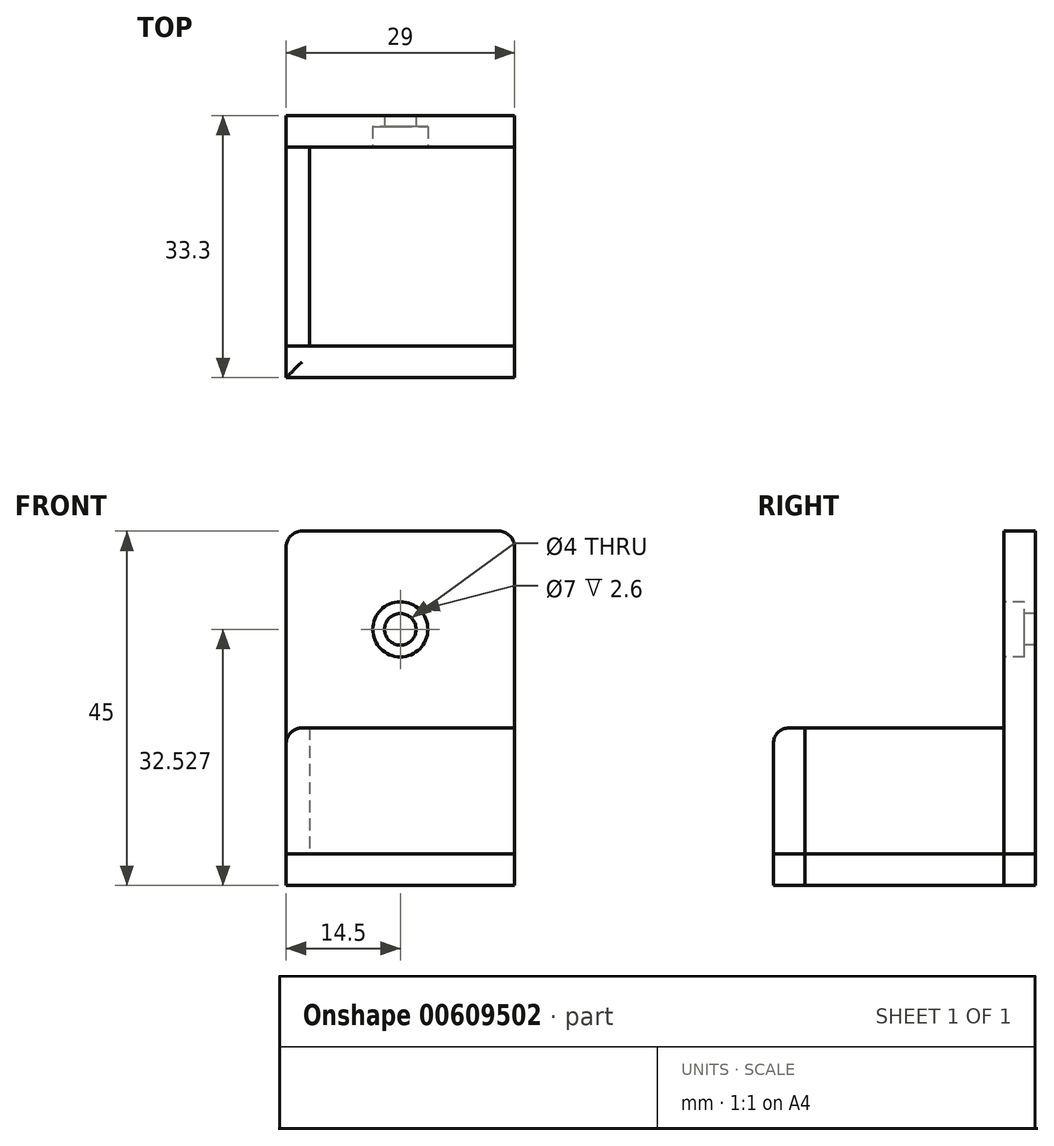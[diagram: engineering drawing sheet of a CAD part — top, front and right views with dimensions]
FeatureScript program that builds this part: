
annotation { "Feature Type Name" : "Feature", "Feature Type Description" : "" }
export const myFeature = defineFeature(function(context is Context, id is Id, definition is map)
    precondition{}
    {
        {
            var Q0;
            Q0=qCreatedBy(makeId("Top.planeOp"),FACE);
            var sketch = newSketch(context, id + "F0", { "sketchPlane" : qUnion([Q0])});
            skLineSegment(sketch, "E0.bottom", {"start": v(14.5, -16.65) * mm, "end": v(-14.5, -16.65) * mm});
            skLineSegment(sketch, "E0.top", {"start": v(14.5, 16.65) * mm, "end": v(-14.5, 16.65) * mm});
            skLineSegment(sketch, "E0.left", {"start": v(14.5, -16.65) * mm, "end": v(14.5, 16.65) * mm});
            skLineSegment(sketch, "E0.right", {"start": v(-14.5, -16.65) * mm, "end": v(-14.5, 16.65) * mm});
            skPoint(sketch, "E0.middle", {"position": v(0, 0) * mm});
            skSolve(sketch);
        }
        {
            var Q0;
            Q0 = qSketchRegion(id + "F0", true);
            extrude(context, id + "F1", {"entities" : qUnion([Q0]), "depth" : 4 * mm, "offsetDistance" : 25 * mm});
        }
        {
            var Q0;
            Q0=makeQuery(id+"F0.imprint","IMPRINT",FACE,{"disambiguationData":[TD([[makeQuery(id+"F0.imprint","IMPRINT",EDGE,{"derivedFrom":sQuery(id+"F0.wireOp",EDGE,"E0.bottom")}),-1.0]])]});
            var sketch = newSketch(context, id + "F2", { "sketchPlane" : qUnion([Q0])});
            skLineSegment(sketch, "E1.bottom", {"start": v(-14.5, 16.65) * mm, "end": v(14.5, 16.65) * mm});
            skLineSegment(sketch, "E1.top", {"start": v(-14.5, 12.65) * mm, "end": v(14.5, 12.65) * mm});
            skLineSegment(sketch, "E1.left", {"start": v(-14.5, 16.65) * mm, "end": v(-14.5, 12.65) * mm});
            skLineSegment(sketch, "E1.right", {"start": v(14.5, 16.65) * mm, "end": v(14.5, 12.65) * mm});
            skSolve(sketch);
        }
        {
            var Q0;
            Q0 = qSketchRegion(id + "F2", true);
            extrude(context, id + "F3", {"entities" : qUnion([Q0]), "depth" : 45 * mm, "offsetDistance" : 25 * mm});
        }
        {
            var Q0;
            Q0=makeQuery(id+"F2.imprint","IMPRINT",FACE,{"disambiguationData":[TD([[makeQuery(id+"F2.imprint","IMPRINT",EDGE,{"derivedFrom":sQuery(id+"F2.wireOp",EDGE,"E1.bottom")}),1.0]])]});
            var sketch = newSketch(context, id + "F4", { "sketchPlane" : qUnion([Q0])});
            skLineSegment(sketch, "E2.bottom", {"start": v(-14.5, -16.65) * mm, "end": v(14.5, -16.65) * mm});
            skLineSegment(sketch, "E2.top", {"start": v(-14.5, -12.65) * mm, "end": v(14.5, -12.65) * mm});
            skLineSegment(sketch, "E2.left", {"start": v(-14.5, -16.65) * mm, "end": v(-14.5, -12.65) * mm});
            skLineSegment(sketch, "E2.right", {"start": v(14.5, -16.65) * mm, "end": v(14.5, -12.65) * mm});
            skSolve(sketch);
        }
        {
            var Q0;
            Q0 = qSketchRegion(id + "F4", true);
            extrude(context, id + "F5", {"entities" : qUnion([Q0]), "depth" : 20 * mm, "offsetDistance" : 25 * mm});
        }
        {
            var Q0;
            Q0=makeQuery(id+"F3.opExtrude","SWEPT_FACE",FACE,{"disambiguationData":[OSD([sQuery(id+"F2.wireOp",EDGE,"E1.top")])]});
            var sketch = newSketch(context, id + "F6", { "sketchPlane" : qUnion([Q0])});
            skCircle(sketch, "E3", {"center": v(0, 32.53) * mm, "radius": 2 * mm});
            skPoint(sketch, "E4", {"position": v(0, 40.1) * mm});
            skSolve(sketch);
        }
        {
            var Q0;
            Q0 = qSketchRegion(id + "F6", true);
            extrude(context, id + "F7", {"entities" : qUnion([Q0]), "operationType" : NewBodyOperationType.REMOVE, "oppositeDirection" : true, "depth" : 6 * mm, "offsetDistance" : 25 * mm});
        }
        {
            var Q0;
            Q0=makeQuery(id+"F3.opExtrude","SWEPT_FACE",FACE,{"disambiguationData":[OSD([sQuery(id+"F2.wireOp",EDGE,"E1.top")])]});
            var sketch = newSketch(context, id + "F8", { "sketchPlane" : qUnion([Q0])});
            skCircle(sketch, "E5", {"center": v(0, 32.53) * mm, "radius": 3.5 * mm});
            skSolve(sketch);
        }
        {
            var Q0;
            Q0 = qSketchRegion(id + "F8", true);
            extrude(context, id + "F9", {"entities" : qUnion([Q0]), "operationType" : NewBodyOperationType.REMOVE, "oppositeDirection" : true, "depth" : 2.6 * mm, "offsetDistance" : 25 * mm});
        }
        {
            var Q0;
            Q0=makeQuery(id+"F3.opExtrude","CAP_EDGE",EDGE,{"disambiguationData":[OSD([sQuery(id+"F2.wireOp",EDGE,"E1.left")])],"isStart":false});
            var Q1;
            Q1=makeQuery(id+"F3.opExtrude","CAP_EDGE",EDGE,{"disambiguationData":[OSD([sQuery(id+"F2.wireOp",EDGE,"E1.right")])],"isStart":false});
            fillet(context, id + "F10", {"entities" : qUnion([Q0, Q1]), "radius" : 2 * mm, "tangentPropagation" : true, "allowEdgeOverflow" : false});
        }
        {
            var Q0;
            Q0=makeQuery(id+"F1.opExtrude","CAP_FACE",FACE,{"disambiguationData":[OSD([sQuery(id+"F0.wireOp",EDGE,"E0.bottom"),sQuery(id+"F0.wireOp",EDGE,"E0.top"),sQuery(id+"F0.wireOp",EDGE,"E0.left"),sQuery(id+"F0.wireOp",EDGE,"E0.right")])],"isStart":false});
            var sketch = newSketch(context, id + "F11", { "sketchPlane" : qUnion([Q0])});
            skLineSegment(sketch, "E6.bottom", {"start": v(-14.5, 12.65) * mm, "end": v(-11.5, 12.65) * mm});
            skLineSegment(sketch, "E6.top", {"start": v(-14.5, -12.65) * mm, "end": v(-11.5, -12.65) * mm});
            skLineSegment(sketch, "E6.left", {"start": v(-14.5, 12.65) * mm, "end": v(-14.5, -12.65) * mm});
            skLineSegment(sketch, "E6.right", {"start": v(-11.5, 12.65) * mm, "end": v(-11.5, -12.65) * mm});
            skSolve(sketch);
        }
        {
            var Q0;
            Q0=makeQuery(id+"F11.imprint","IMPRINT",FACE,{"disambiguationData":[TD([[makeQuery(id+"F11.imprint","IMPRINT",EDGE,{"derivedFrom":sQuery(id+"F11.wireOp",EDGE,"E6.bottom")}),-1.0]])]});
            extrude(context, id + "F12", {"entities" : qUnion([Q0]), "depth" : 16 * mm, "offsetDistance" : 25 * mm});
        }
        {
            var Q0;
            Q0=makeQuery(id+"F5.opExtrude","CAP_EDGE",EDGE,{"disambiguationData":[OSD([sQuery(id+"F4.wireOp",EDGE,"E2.bottom")])],"isStart":false});
            var Q1;
            Q1=makeQuery(id+"F12.opExtrude","CAP_EDGE",EDGE,{"disambiguationData":[OSD([sQuery(id+"F11.wireOp",EDGE,"E6.left")])],"isStart":false});
            var Q2;
            Q2=makeQuery(id+"F5.opExtrude","CAP_EDGE",EDGE,{"disambiguationData":[OSD([sQuery(id+"F4.wireOp",EDGE,"E2.left")])],"isStart":false});
            fillet(context, id + "F13", {"entities" : qUnion([Q0, Q1, Q2]), "radius" : 2 * mm, "tangentPropagation" : true, "allowEdgeOverflow" : false});
        }
    });
